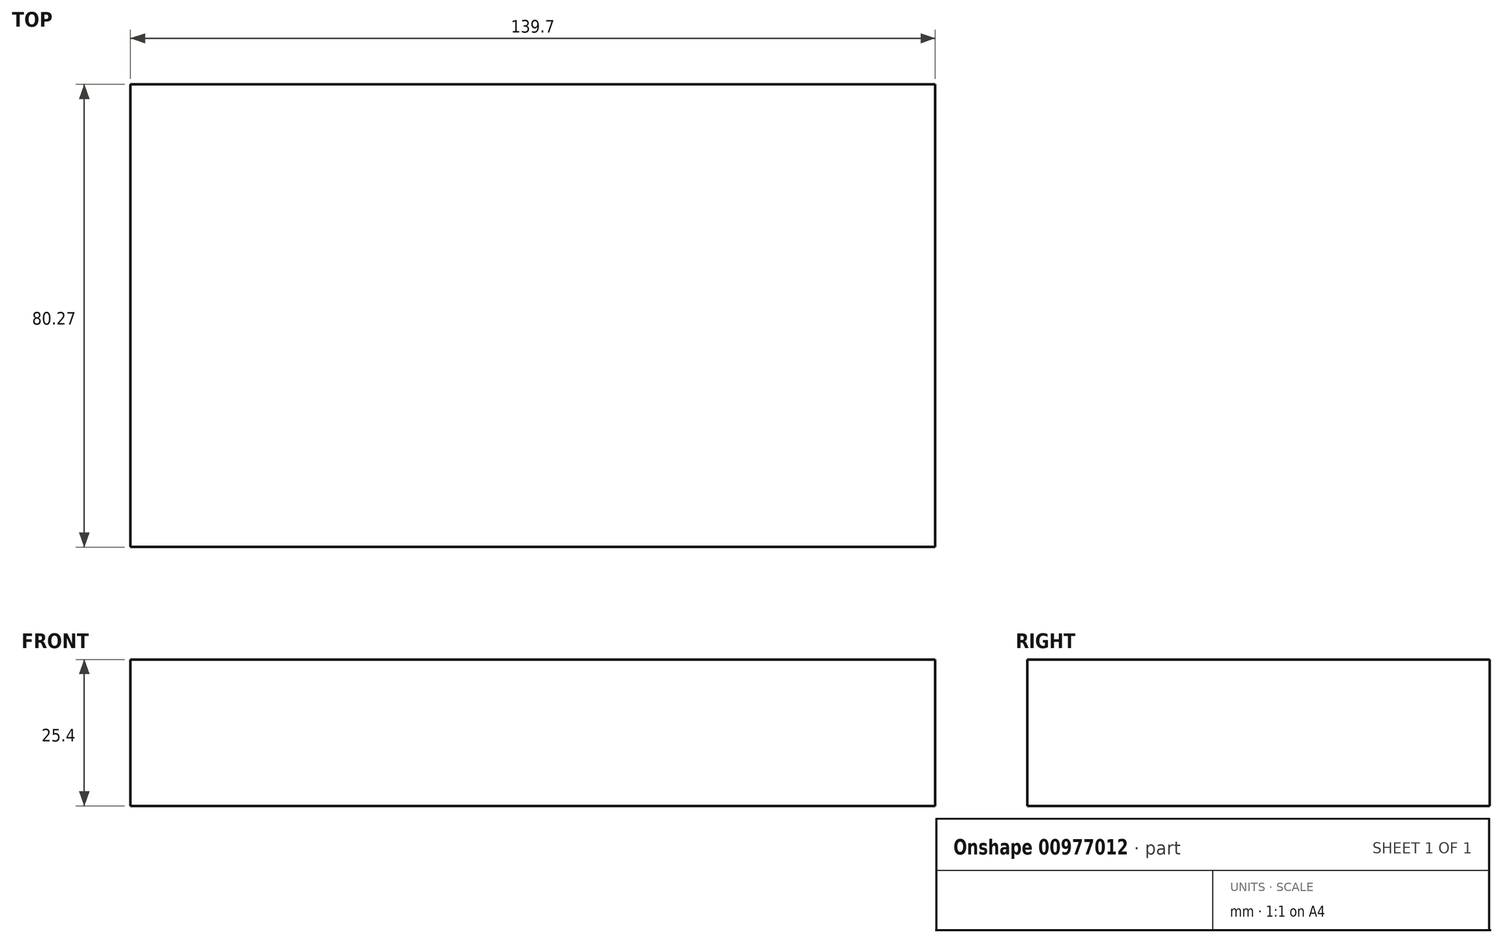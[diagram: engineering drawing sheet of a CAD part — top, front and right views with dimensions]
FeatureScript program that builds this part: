
annotation { "Feature Type Name" : "Feature", "Feature Type Description" : "" }
export const myFeature = defineFeature(function(context is Context, id is Id, definition is map)
    precondition{}
    {
        {
            var Q0;
            Q0=qCreatedBy(makeId("Top.planeOp"),FACE);
            var sketch = newSketch(context, id + "F0", { "sketchPlane" : qUnion([Q0])});
            skLineSegment(sketch, "E0.bottom", {"start": v(-87.06, 58.87) * mm, "end": v(52.64, 58.87) * mm});
            skLineSegment(sketch, "E0.top", {"start": v(-87.06, -21.4) * mm, "end": v(52.64, -21.4) * mm});
            skLineSegment(sketch, "E0.left", {"start": v(-87.06, 58.87) * mm, "end": v(-87.06, -21.4) * mm});
            skLineSegment(sketch, "E0.right", {"start": v(52.64, 58.87) * mm, "end": v(52.64, -21.4) * mm});
            skSolve(sketch);
        }
        {
            var Q0;
            Q0 = qSketchRegion(id + "F0", true);
            extrude(context, id + "F1", {"entities" : qUnion([Q0]), "depth" : 25.4 * mm, "offsetDistance" : 25.4 * mm});
        }
    });
